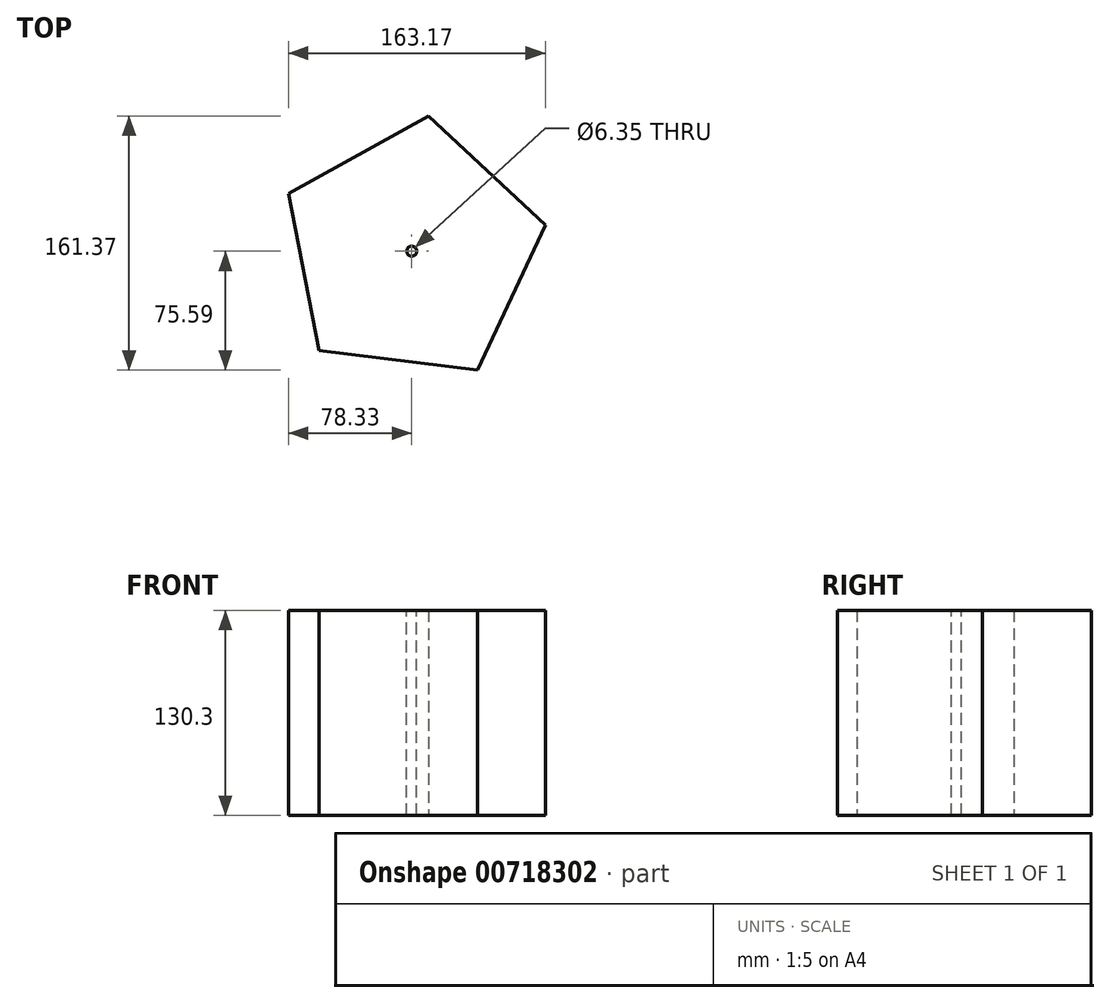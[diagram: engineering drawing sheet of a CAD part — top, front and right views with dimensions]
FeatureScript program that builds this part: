
annotation { "Feature Type Name" : "Feature", "Feature Type Description" : "" }
export const myFeature = defineFeature(function(context is Context, id is Id, definition is map)
    precondition{}
    {
        {
            var Q0;
            Q0=qCreatedBy(makeId("Top.planeOp"),FACE);
            var sketch = newSketch(context, id + "F0", { "sketchPlane" : qUnion([Q0])});
            skCircle(sketch, "E0.cCircle", {"center": v(0, 0) * mm, "radius": 69.92 * mm, "construction": true});
            skLineSegment(sketch, "E0.0", {"start": v(-78.33, 36.52) * mm, "end": v(10.53, 85.78) * mm});
            skLineSegment(sketch, "E0.1", {"start": v(10.53, 85.78) * mm, "end": v(84.84, 16.5) * mm});
            skLineSegment(sketch, "E0.2", {"start": v(84.84, 16.5) * mm, "end": v(41.9, -75.59) * mm});
            skLineSegment(sketch, "E0.3", {"start": v(41.9, -75.59) * mm, "end": v(-58.94, -63.21) * mm});
            skLineSegment(sketch, "E0.4", {"start": v(-58.94, -63.21) * mm, "end": v(-78.33, 36.52) * mm});
            skPoint(sketch, "E0.0.midPoint", {"position": v(-33.9, 61.15) * mm});
            skSolve(sketch);
        }
        {
            var Q0;
            Q0 = qSketchRegion(id + "F0", true);
            extrude(context, id + "F1", {"entities" : qUnion([Q0]), "depth" : 130.3 * mm, "offsetDistance" : 25.4 * mm});
        }
        {
            var Q0;
            Q0=makeQuery(id+"F1.opExtrude","CAP_FACE",FACE,{"disambiguationData":[OSD([sQuery(id+"F0.wireOp",EDGE,"E0.0"),sQuery(id+"F0.wireOp",EDGE,"E0.1"),sQuery(id+"F0.wireOp",EDGE,"E0.2"),sQuery(id+"F0.wireOp",EDGE,"E0.3"),sQuery(id+"F0.wireOp",EDGE,"E0.4")])],"isStart":false});
            var sketch = newSketch(context, id + "F2", { "sketchPlane" : qUnion([Q0])});
            skCircle(sketch, "E1", {"center": v(0, 0) * mm, "radius": 19.05 * mm});
            skSolve(sketch);
        }
        {
            var Q0;
            Q0=sQuery(id+"F2.wireOp",VERTEX,"E1.center");
            var Q1;
            Q1=makeQuery(id+"F1.opExtrude","SWEPT_BODY",BODY,{"disambiguationData":[OSD([sQuery(id+"F0.wireOp",EDGE,"E0.0"),sQuery(id+"F0.wireOp",EDGE,"E0.1"),sQuery(id+"F0.wireOp",EDGE,"E0.2"),sQuery(id+"F0.wireOp",EDGE,"E0.3"),sQuery(id+"F0.wireOp",EDGE,"E0.4")])]});
            hole(context, id + "F3", {"style" : HoleStyle.SIMPLE, "endStyle" : HoleEndStyle.THROUGH, "holeDiameter" : 6.35 * mm, "majorDiameter" : 6.35 * mm, "isTappedThrough" : true, "tappedDepth" : 12.7 * mm, "tapClearance" : 3, "locations" : qUnion([Q0]), "scope" : qUnion([Q1])});
        }
    });
